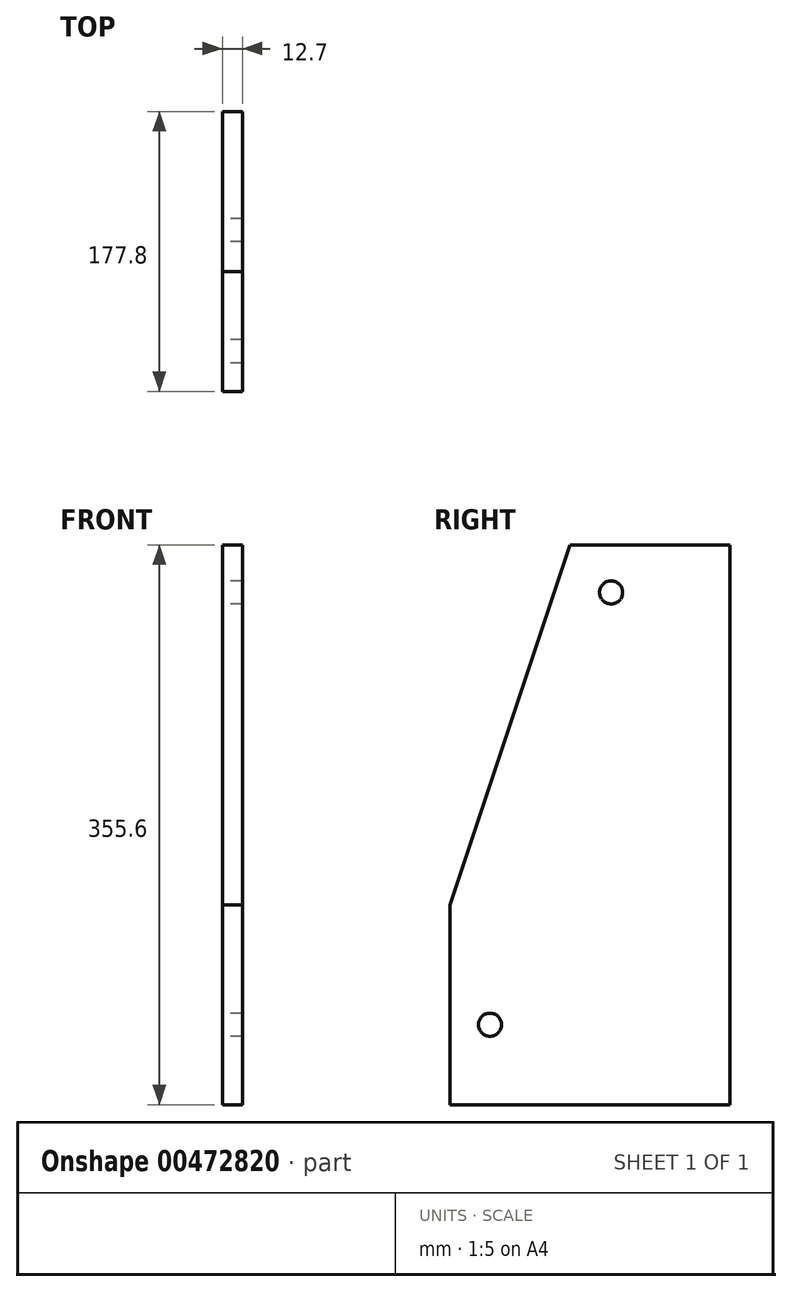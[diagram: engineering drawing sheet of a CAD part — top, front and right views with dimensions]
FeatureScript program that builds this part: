
annotation { "Feature Type Name" : "Feature", "Feature Type Description" : "" }
export const myFeature = defineFeature(function(context is Context, id is Id, definition is map)
    precondition{}
    {
        {
            var Q0;
            Q0=qCreatedBy(makeId("Right.planeOp"),FACE);
            var sketch = newSketch(context, id + "F0", { "sketchPlane" : qUnion([Q0])});
            skLineSegment(sketch, "E0", {"start": v(0, 0) * mm, "end": v(177.8, 0) * mm});
            skLineSegment(sketch, "E1", {"start": v(177.8, 0) * mm, "end": v(177.8, 355.6) * mm});
            skLineSegment(sketch, "E2", {"start": v(177.8, 355.6) * mm, "end": v(76.2, 355.6) * mm});
            skCircle(sketch, "E3", {"center": v(102.37, 325.38) * mm, "radius": 7.33 * mm});
            skCircle(sketch, "E4", {"center": v(25.4, 50.8) * mm, "radius": 7.33 * mm});
            skLineSegment(sketch, "E5", {"start": v(0, 0) * mm, "end": v(0, 127) * mm});
            skLineSegment(sketch, "E6", {"start": v(0, 127) * mm, "end": v(76.2, 355.6) * mm});
            skSolve(sketch);
        }
        {
            var Q0;
            Q0=makeQuery(id+"F0.imprint","IMPRINT",FACE,{"disambiguationData":[TD([[makeQuery(id+"F0.imprint","IMPRINT",EDGE,{"derivedFrom":sQuery(id+"F0.wireOp",EDGE,"E0")}),1.0]])]});
            extrude(context, id + "F1", {"entities" : qUnion([Q0]), "depth" : 12.7 * mm});
        }
    });
